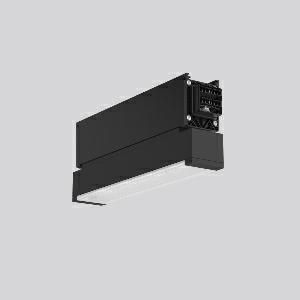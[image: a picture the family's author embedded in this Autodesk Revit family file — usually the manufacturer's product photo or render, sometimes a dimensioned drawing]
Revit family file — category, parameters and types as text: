
# Revit family: linedo_module_rt_9503rt_763_437_00c_b91e
name_source: partatom
category: Lighting Fixtures
units: mm (PartAtom-declared; Revit-internal decimal feet)

## family parameters
Cut with Voids When Loaded = No
Host = Face
Light Source = No
Part Type = Normal
Room Calculation Point = No
Round Connector Dimension = Use Diameter
Shared = No

## types (1)
- LINEDO Module RT (1 x LED Modul 763, 480 lm, 6300)
    Apparent Load = 6 VA
    CIE Flux Codes = 86 96 99 99 100
    Color Rendering = 70
    Color Temperature = 6300
    Default Elevation = 1800 mm
    Description = LINEDO, 6 W, 480 lm, 763, black, on/off
Continuous line luminaire, L 342 B 58 H 131, SBS, 3 h, emergency-220 lm, DALI-Sibe
    Height = 131 mm
    Lamp = 1 x LED Modul 763
    Lamp Light Flux = 480 lm
    Lamp count = 1
    Length = 342 mm
    Lifetime = 50000 h
    Luminous efficacy = 80 lm/W
    Manufacturer = RZB
    ModVariant = No
    Model = 9503RT.763.437.00C
    Mounting Place = Ceiling
    Mounting Type = Surface mounted
    Number of Poles = 1
    OnlyDefault = Yes
    Power Factor = 1
    Product Name = LINEDO Module RT
    Product group = Surface mounted continuous line luminaire system
    ProductGroupID = 310
    Protection Class = Protection class I
    Protection Degree = IP 54
    RLX_Detail_Level = 1
    RLX_Emergency_Light_Flux = 220 lm
    RLX_Emergency_Type = 3
    RLX_Emergency_Type_DB = Yes
    RlxData = <blob elided: 20221 chars, md5=d3c4ecfc>
    Socket = socket
    Standby Power = 0 W
    System Light Flux = 480 lm
    System Power = 6 W
    Type Comments = Product without accessories
    Type Image = 9503rf.763.430.00c.jpg
    URL = http://relux.com
    VarID = ---
    Voltage = 230 V
    Voltage Range = 220-240 V
    Weight = 0.00 kg
    Width = 58 mm

## geometry (parser evidence)
native form markers: Blend x4, Sweep x12
no freeform markers — native parametric forms only
